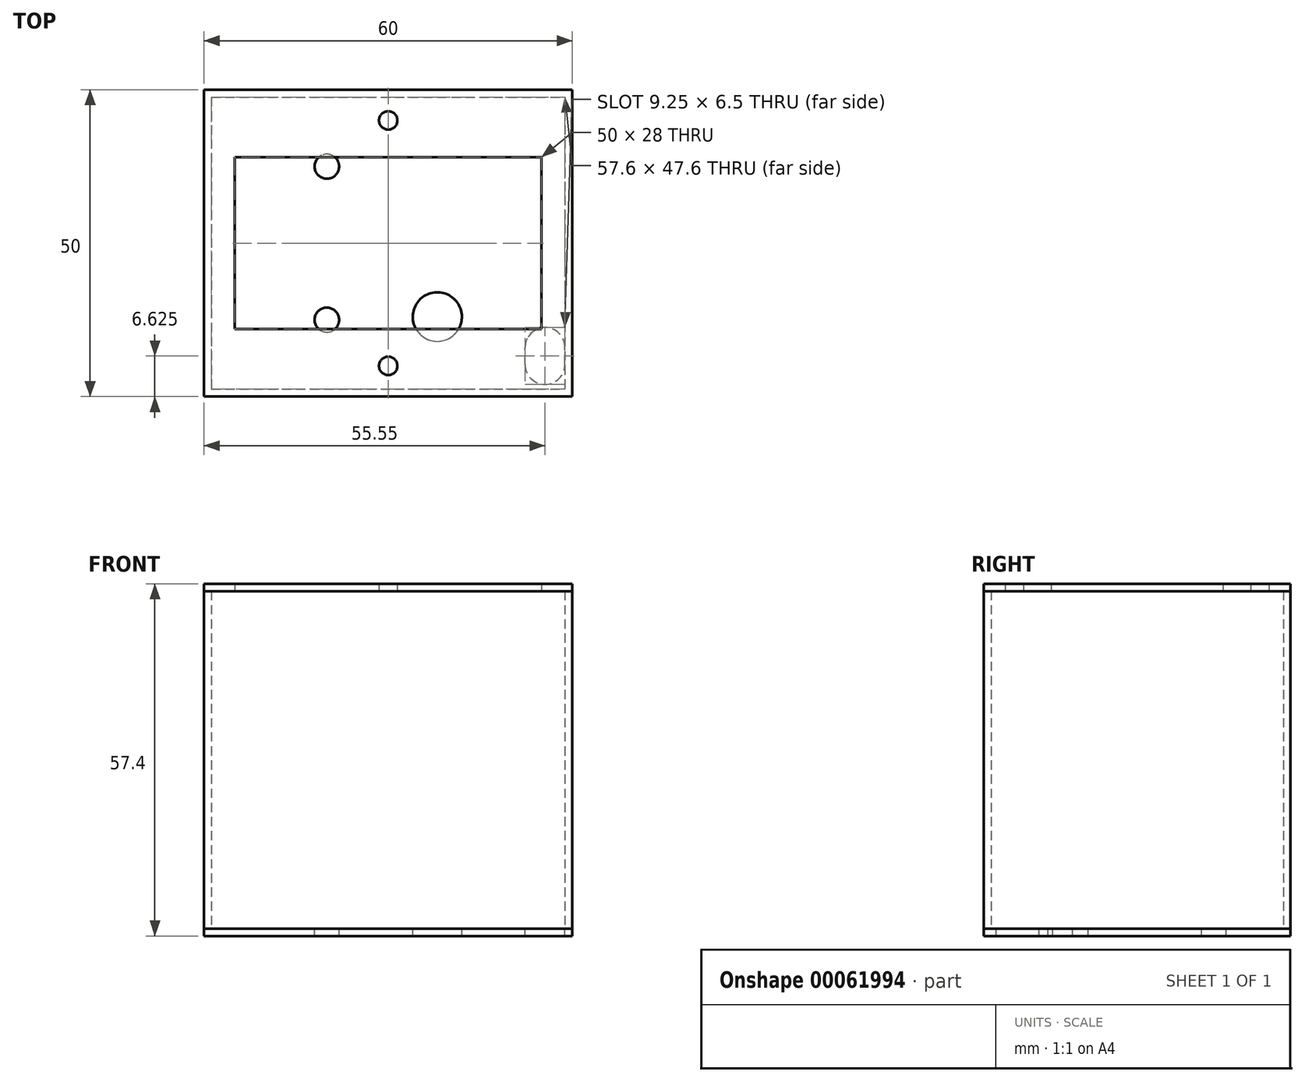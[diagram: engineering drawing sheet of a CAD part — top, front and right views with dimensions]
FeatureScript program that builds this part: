
annotation { "Feature Type Name" : "Feature", "Feature Type Description" : "" }
export const myFeature = defineFeature(function(context is Context, id is Id, definition is map)
    precondition{}
    {
        {
            var Q0;
            Q0=qCreatedBy(makeId("Top.planeOp"),FACE);
            var sketch = newSketch(context, id + "F0", { "sketchPlane" : qUnion([Q0])});
            skLineSegment(sketch, "E0.rect.bottom", {"start": v(-30, 25) * mm, "end": v(30, 25) * mm});
            skLineSegment(sketch, "E0.rect.top", {"start": v(-30, -25) * mm, "end": v(30, -25) * mm});
            skLineSegment(sketch, "E0.rect.left", {"start": v(-30, 25) * mm, "end": v(-30, -25) * mm});
            skLineSegment(sketch, "E0.rect.right", {"start": v(30, 25) * mm, "end": v(30, -25) * mm});
            skPoint(sketch, "E0.rect.middle", {"position": v(0, 0) * mm});
            skLineSegment(sketch, "E1.rect.bottom", {"start": v(-28.8, 23.8) * mm, "end": v(28.8, 23.8) * mm});
            skLineSegment(sketch, "E1.rect.top", {"start": v(-28.8, -23.8) * mm, "end": v(28.8, -23.8) * mm});
            skLineSegment(sketch, "E1.rect.left", {"start": v(-28.8, 23.8) * mm, "end": v(-28.8, -23.8) * mm});
            skLineSegment(sketch, "E1.rect.right", {"start": v(28.8, 23.8) * mm, "end": v(28.8, -23.8) * mm});
            skSolve(sketch);
        }
        {
            var Q0;
            Q0=makeQuery(id+"F0.imprint","IMPRINT",FACE,{"disambiguationData":[TD([[makeQuery(id+"F0.imprint","IMPRINT",EDGE,{"derivedFrom":sQuery(id+"F0.wireOp",EDGE,"E0.rect.bottom")}),-1.0]])]});
            extrude(context, id + "F1", {"entities" : qUnion([Q0]), "depth" : 55 * mm});
        }
        {
            var Q0;
            Q0=makeQuery(id+"F1.opExtrude","CAP_FACE",FACE,{"disambiguationData":[OSD([sQuery(id+"F0.wireOp",EDGE,"E0.rect.bottom"),sQuery(id+"F0.wireOp",EDGE,"E0.rect.top"),sQuery(id+"F0.wireOp",EDGE,"E0.rect.left"),sQuery(id+"F0.wireOp",EDGE,"E0.rect.right")])],"isStart":false});
            var sketch = newSketch(context, id + "F2", { "sketchPlane" : qUnion([Q0])});
            skLineSegment(sketch, "E2.rect.bottom", {"start": v(-25, 14) * mm, "end": v(25, 14) * mm});
            skLineSegment(sketch, "E2.rect.top", {"start": v(-25, -14) * mm, "end": v(25, -14) * mm});
            skLineSegment(sketch, "E2.rect.left", {"start": v(-25, 14) * mm, "end": v(-25, -14) * mm});
            skLineSegment(sketch, "E2.rect.right", {"start": v(25, 14) * mm, "end": v(25, -14) * mm});
            skPoint(sketch, "E2.rect.middle", {"position": v(0, 0) * mm});
            skLineSegment(sketch, "E3.0", {"start": v(-30, 25) * mm, "end": v(-30, -25) * mm});
            skLineSegment(sketch, "E3.1", {"start": v(-30, 25) * mm, "end": v(30, 25) * mm});
            skLineSegment(sketch, "E3.2", {"start": v(30, 25) * mm, "end": v(30, -25) * mm});
            skLineSegment(sketch, "E3.3", {"start": v(-30, -25) * mm, "end": v(30, -25) * mm});
            skCircle(sketch, "E4", {"center": v(0, -20) * mm, "radius": 1.5 * mm});
            skCircle(sketch, "E5", {"center": v(0, 20) * mm, "radius": 1.5 * mm});
            skSolve(sketch);
        }
        {
            var Q0;
            Q0 = qSketchRegion(id + "F2", true);
            extrude(context, id + "F3", {"entities" : qUnion([Q0]), "depth" : 1.2 * mm});
        }
        {
            var Q0;
            Q0=qCreatedBy(makeId("Top.planeOp"),FACE);
            var sketch = newSketch(context, id + "F4", { "sketchPlane" : qUnion([Q0])});
            skLineSegment(sketch, "E6.0", {"start": v(-30, 25) * mm, "end": v(-30, -25) * mm});
            skLineSegment(sketch, "E6.1", {"start": v(-30, -25) * mm, "end": v(30, -25) * mm});
            skLineSegment(sketch, "E6.2", {"start": v(30, 25) * mm, "end": v(30, -25) * mm});
            skLineSegment(sketch, "E6.3", {"start": v(-30, 25) * mm, "end": v(30, 25) * mm});
            skCircle(sketch, "E7", {"center": v(-10, -12.5) * mm, "radius": 2 * mm});
            skCircle(sketch, "E8", {"center": v(-10, 12.5) * mm, "radius": 2 * mm});
            skCircle(sketch, "E9", {"center": v(8, -12) * mm, "radius": 4 * mm});
            skLineSegment(sketch, "E10.0", {"start": v(-28.8, -23.8) * mm, "end": v(28.8, -23.8) * mm, "construction": true});
            skLineSegment(sketch, "E11.0", {"start": v(28.8, 23.8) * mm, "end": v(28.8, -23.8) * mm, "construction": true});
            skLineSegment(sketch, "E12.rect.left", {"start": v(28.8, -19.75) * mm, "end": v(28.8, -17) * mm});
            skLineSegment(sketch, "E12.rect.right", {"start": v(22.3, -19.75) * mm, "end": v(22.3, -17) * mm});
            skPoint(sketch, "E12.rect.middle", {"position": v(25.55, -18.37) * mm});
            skArc(sketch, "E13", {"start": v(22.3, -19.75) * mm, "mid": v(25.55, -23) * mm, "end": v(28.8, -19.75) * mm});
            skPoint(sketch, "E13.centerSnap0", {"position": v(25.55, -19.75) * mm});
            skArc(sketch, "E14", {"start": v(28.8, -17) * mm, "mid": v(25.55, -13.75) * mm, "end": v(22.3, -17) * mm});
            skPoint(sketch, "E14.centerSnap0", {"position": v(25.55, -17) * mm});
            skSolve(sketch);
        }
        {
            var Q0;
            Q0 = qSketchRegion(id + "F4", true);
            extrude(context, id + "F5", {"entities" : qUnion([Q0]), "oppositeDirection" : true, "depth" : 1.2 * mm});
        }
    });
